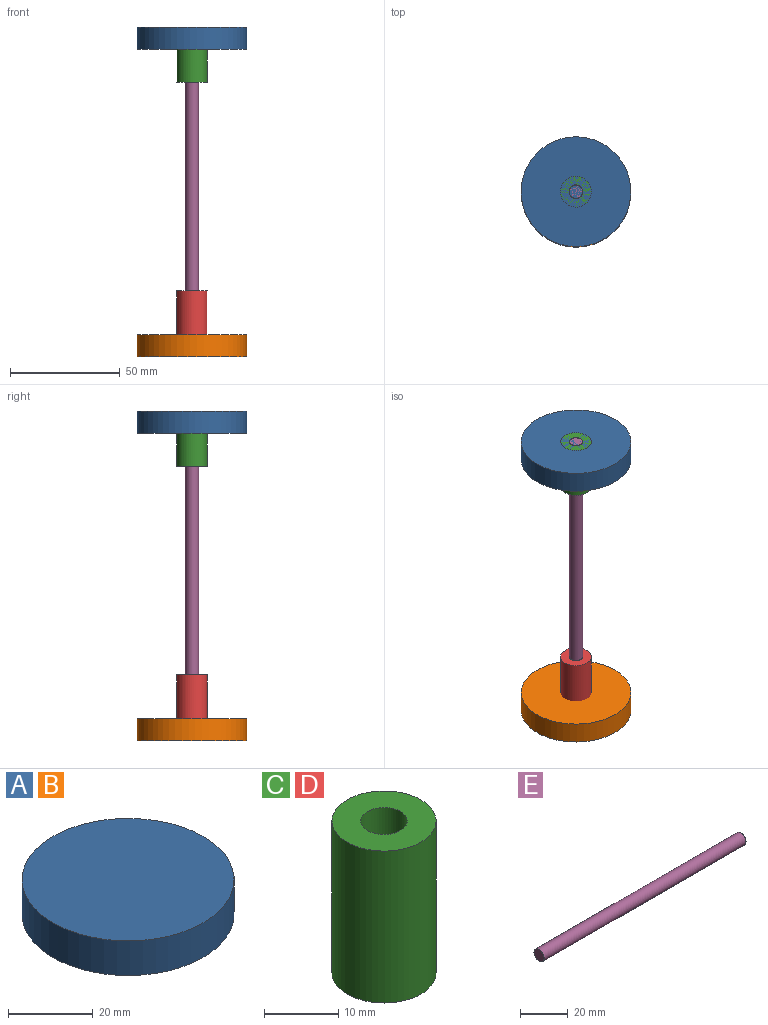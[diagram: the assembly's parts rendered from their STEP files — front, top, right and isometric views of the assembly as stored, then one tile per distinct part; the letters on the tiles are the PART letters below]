
ASSEMBLY  parts=5 mates=3
PART A: 3 faces, bbox 50x50x10 mm
  f0: cylinder r=25mm len=50mm, axis (0,0,1), area 1570.8mm2, adj f1,f2
  f1: plane 50x50mm, normal (0,0,-1), area 1963.5mm2, adj f0
  f2: plane 50x50mm, normal (0,0,1), area 1963.5mm2, adj f0
PART B: same geometry as A
PART C: 4 faces, bbox 14x14x25 mm
  f0: cylinder r=3.12mm len=25mm, axis (0,0,-1), area 490.9mm2, adj f2,f3
  f1: cylinder r=7mm len=25mm, axis (0,0,-1), area 1099.6mm2, adj f2,f3
  f2: plane 14x14mm, normal (0,0,1), area 123.3mm2, adj f0,f1
  f3: plane 14x14mm, normal (0,0,-1), area 123.3mm2, adj f0,f1
PART D: same geometry as C
PART E: 3 faces, bbox 120x6x6 mm
  f0: plane 6x6mm, normal (-1,0,0), area 28.3mm2, adj f1
  f1: cylinder r=3mm len=120mm, axis (-1,0,0), area 2261.9mm2, adj f0,f2
  f2: plane 6x6mm, normal (1,0,0), area 28.3mm2, adj f1
PLACE A t=(33.47,-26.36,149.35)mm
PLACE B t=(33.47,-26.36,9.45)mm
PLACE C t=(33.47,-26.36,124.35)mm
PLACE D rot(axis=(0,0,1),180deg) t=(33.47,-26.36,4.35)mm
PLACE E rot(axis=(0,1,0),90deg) t=(31.97,-26.36,89.35)mm
MATE planar C.f0 <-> E.f1  axis (0,0,1) through (33.47,-26.36,149.35)mm
MATE fastened E.f1 <-> D.f1  axis (0,0,-1) through (33.47,-26.36,29.35)mm
MATE planar E.f1 <-> A.f0  axis (0,0,1) through (33.47,-26.36,149.35)mm
